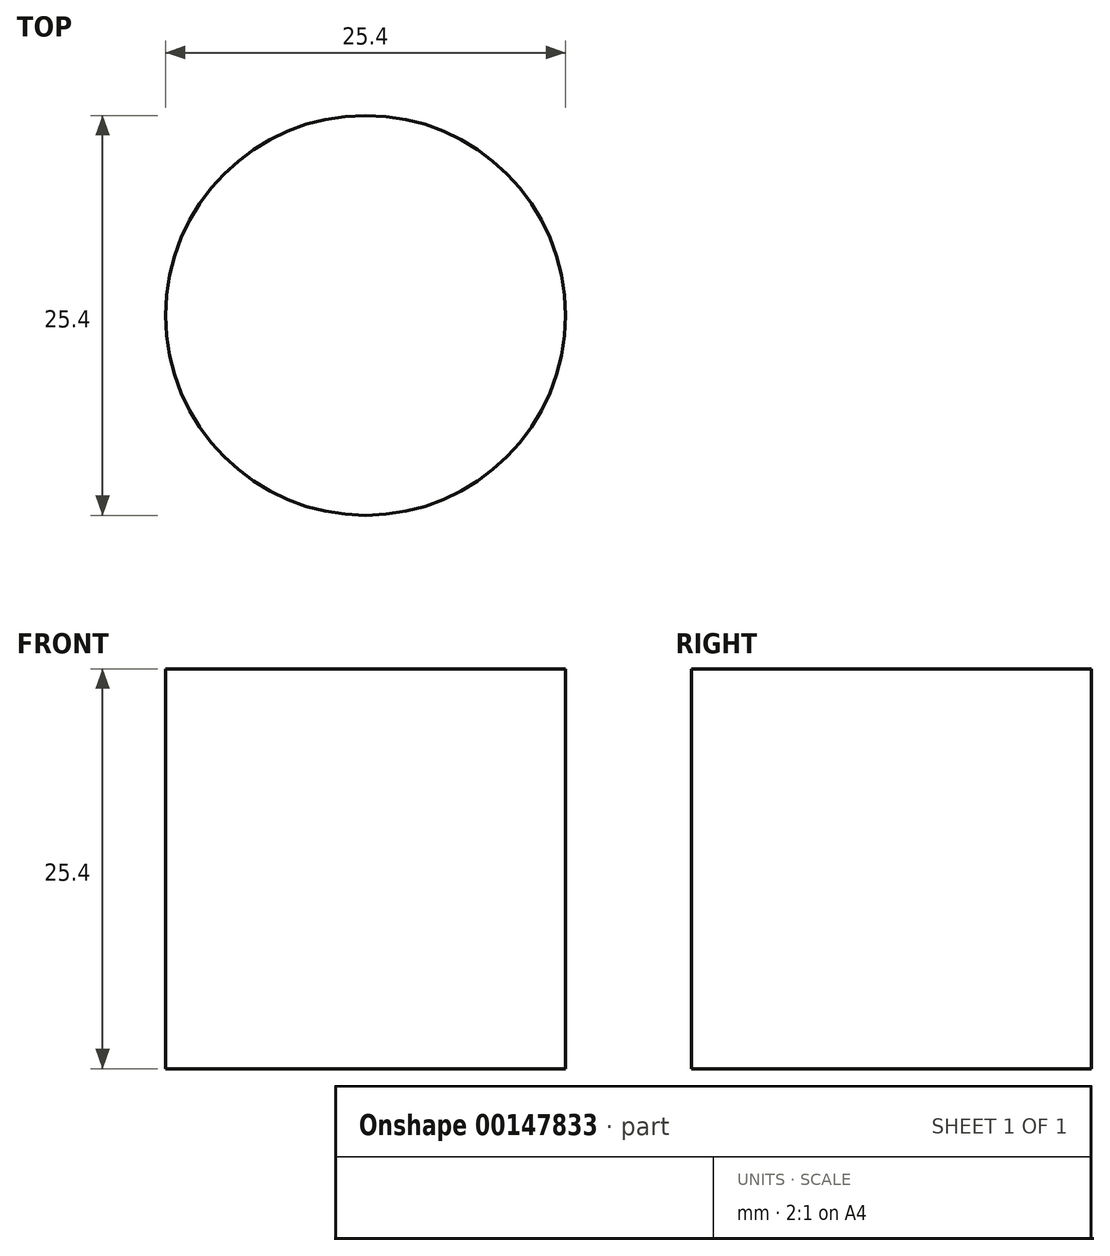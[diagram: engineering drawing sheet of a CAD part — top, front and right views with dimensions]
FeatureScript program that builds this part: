
annotation { "Feature Type Name" : "Feature", "Feature Type Description" : "" }
export const myFeature = defineFeature(function(context is Context, id is Id, definition is map)
    precondition{}
    {
        {
            var Q0;
            Q0=qCreatedBy(makeId("Top.planeOp"),FACE);
            var sketch = newSketch(context, id + "F0", { "sketchPlane" : qUnion([Q0])});
            skLineSegment(sketch, "E0.bottom", {"start": v(0, 0) * mm, "end": v(442.41, 0) * mm, "construction": true});
            skLineSegment(sketch, "E0.top", {"start": v(0, 304.8) * mm, "end": v(442.41, 304.8) * mm, "construction": true});
            skLineSegment(sketch, "E0.left", {"start": v(0, 0) * mm, "end": v(0, 304.8) * mm, "construction": true});
            skLineSegment(sketch, "E0.right", {"start": v(442.41, 0) * mm, "end": v(442.41, 304.8) * mm, "construction": true});
            skLineSegment(sketch, "E1", {"start": v(442.41, 152.4) * mm, "end": v(417.01, 152.4) * mm, "construction": true});
            skLineSegment(sketch, "E2", {"start": v(417.01, 152.4) * mm, "end": v(417.01, 449.16) * mm, "construction": true});
            skLineSegment(sketch, "E3", {"start": v(417.01, 449.16) * mm, "end": v(424.2, 724.58) * mm, "construction": true});
            skLineSegment(sketch, "E4", {"start": v(424.2, 724.58) * mm, "end": v(431.4, 1000) * mm, "construction": true});
            skLineSegment(sketch, "E5", {"start": v(431.4, 1000) * mm, "end": v(579.22, 1000) * mm, "construction": true});
            skLineSegment(sketch, "E6.bottom", {"start": v(579.22, 1015.87) * mm, "end": v(655.42, 1015.87) * mm, "construction": true});
            skLineSegment(sketch, "E6.top", {"start": v(579.22, 984.12) * mm, "end": v(655.42, 984.12) * mm, "construction": true});
            skLineSegment(sketch, "E6.left", {"start": v(579.22, 1015.87) * mm, "end": v(579.22, 984.13) * mm, "construction": true});
            skLineSegment(sketch, "E6.right", {"start": v(655.42, 1015.87) * mm, "end": v(655.42, 984.12) * mm, "construction": true});
            skLineSegment(sketch, "E7", {"start": v(655.42, 1000) * mm, "end": v(680.82, 1000) * mm, "construction": true});
            skLineSegment(sketch, "E8.bottom", {"start": v(680.82, 1009.52) * mm, "end": v(718.92, 1009.52) * mm, "construction": true});
            skLineSegment(sketch, "E8.top", {"start": v(680.82, 990.47) * mm, "end": v(718.92, 990.47) * mm, "construction": true});
            skLineSegment(sketch, "E8.left", {"start": v(680.82, 1009.53) * mm, "end": v(680.82, 990.47) * mm, "construction": true});
            skLineSegment(sketch, "E8.right", {"start": v(718.92, 1009.53) * mm, "end": v(718.92, 990.47) * mm, "construction": true});
            skLineSegment(sketch, "E9.bottom", {"start": v(680.82, 950) * mm, "end": v(1280.82, 950) * mm, "construction": true});
            skLineSegment(sketch, "E9.top", {"start": v(680.82, 1050) * mm, "end": v(1280.82, 1050) * mm, "construction": true});
            skLineSegment(sketch, "E9.right", {"start": v(1280.82, 950) * mm, "end": v(1280.82, 1050) * mm, "construction": true});
            skLineSegment(sketch, "E10", {"start": v(680.82, 1009.53) * mm, "end": v(680.82, 1050) * mm, "construction": true});
            skLineSegment(sketch, "E11", {"start": v(680.82, 990.47) * mm, "end": v(680.82, 950) * mm, "construction": true});
            skCircle(sketch, "E12", {"center": v(0, 0) * mm, "radius": 12.7 * mm});
            skLineSegment(sketch, "E13.bottom", {"start": v(680.82, 0) * mm, "end": v(1280.82, 0) * mm, "construction": true});
            skLineSegment(sketch, "E14", {"start": v(680.82, 0) * mm, "end": v(680.82, 950) * mm, "construction": true});
            skLineSegment(sketch, "E15", {"start": v(1280.82, 0) * mm, "end": v(1280.82, 950) * mm, "construction": true});
            skLineSegment(sketch, "E16", {"start": v(442.41, 0) * mm, "end": v(680.82, 0) * mm, "construction": true});
            skLineSegment(sketch, "E17", {"start": v(680.82, 0) * mm, "end": v(680.82, 0) * mm});
            skLineSegment(sketch, "E18", {"start": v(417.01, 449.16) * mm, "end": v(431.68, 423.76) * mm, "construction": true});
            skLineSegment(sketch, "E19", {"start": v(417.01, 449.16) * mm, "end": v(402.35, 423.76) * mm, "construction": true});
            skLineSegment(sketch, "E20", {"start": v(402.35, 423.76) * mm, "end": v(431.68, 423.76) * mm, "construction": true});
            skPoint(sketch, "E21", {"position": v(417.01, 423.76) * mm});
            skLineSegment(sketch, "E22", {"start": v(424.2, 724.58) * mm, "end": v(438.2, 698.8) * mm, "construction": true});
            skLineSegment(sketch, "E23", {"start": v(424.2, 724.58) * mm, "end": v(408.88, 699.57) * mm, "construction": true});
            skLineSegment(sketch, "E24", {"start": v(408.88, 699.57) * mm, "end": v(438.2, 698.8) * mm, "construction": true});
            skPoint(sketch, "E25", {"position": v(423.54, 699.19) * mm});
            skLineSegment(sketch, "E26", {"start": v(431.4, 1000) * mm, "end": v(445.4, 974.23) * mm, "construction": true});
            skLineSegment(sketch, "E27", {"start": v(445.4, 974.23) * mm, "end": v(416.07, 975) * mm, "construction": true});
            skLineSegment(sketch, "E28", {"start": v(416.07, 975) * mm, "end": v(431.4, 1000) * mm, "construction": true});
            skPoint(sketch, "E29", {"position": v(430.73, 974.6) * mm});
            skCircle(sketch, "E30", {"center": v(442.41, 304.8) * mm, "radius": 32.54 * mm, "construction": true});
            skSolve(sketch);
        }
        {
            var Q0;
            Q0=qSketchRegion(id+"F0",true);
            extrude(context, id + "F1", {"entities" : qUnion([Q0]), "depth" : 25.4 * mm});
        }
    });
